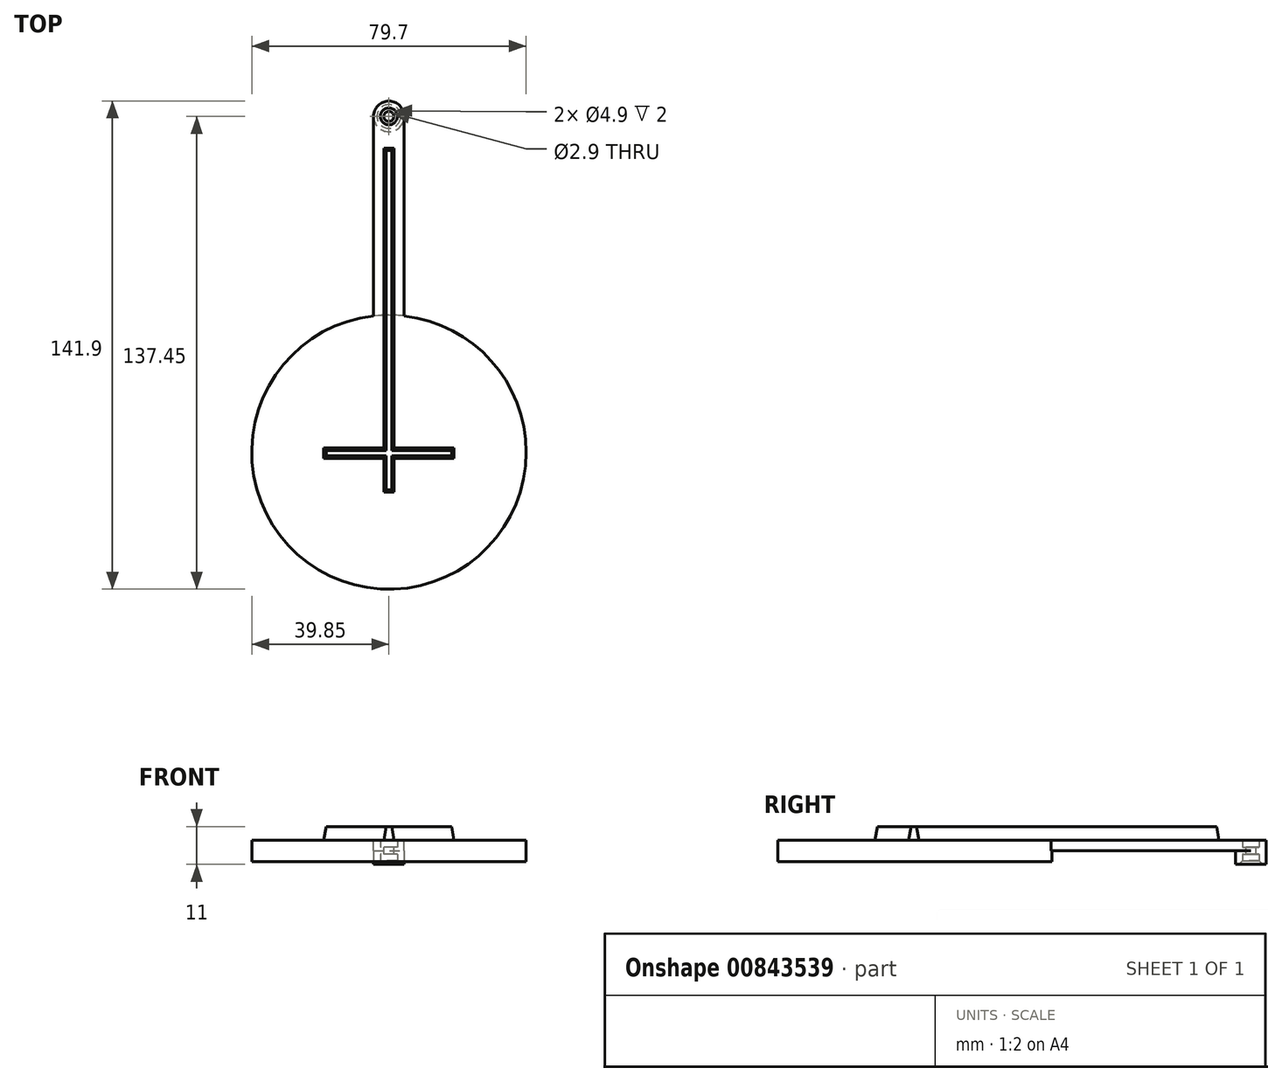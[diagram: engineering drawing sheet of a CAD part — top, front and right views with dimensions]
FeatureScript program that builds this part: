
annotation { "Feature Type Name" : "Feature", "Feature Type Description" : "" }
export const myFeature = defineFeature(function(context is Context, id is Id, definition is map)
    precondition{}
    {
        {
            var Q0;
            Q0=qCreatedBy(makeId("Top.planeOp"),FACE);
            var sketch = newSketch(context, id + "F0", { "sketchPlane" : qUnion([Q0])});
            skCircle(sketch, "E0", {"center": v(0, 0) * mm, "radius": 2.45 * mm});
            skCircle(sketch, "E1", {"center": v(0, 0) * mm, "radius": 4.45 * mm});
            skSolve(sketch);
        }
        {
            var Q0;
            Q0=makeQuery(id+"F0.imprint","IMPRINT",FACE,{"disambiguationData":[TD([[makeQuery(id+"F0.imprint","IMPRINT",EDGE,{"derivedFrom":sQuery(id+"F0.wireOp",EDGE,"E0")}),-1.0]])]});
            extrude(context, id + "F1", {"entities" : qUnion([Q0]), "depth" : 7 * mm, "offsetDistance" : 25 * mm});
        }
        {
            var Q0;
            Q0=makeQuery(id+"F1.opExtrude","CAP_FACE",FACE,{"disambiguationData":[OSD([sQuery(id+"F0.wireOp",EDGE,"E0"),sQuery(id+"F0.wireOp",EDGE,"E1")])],"isStart":false});
            var sketch = newSketch(context, id + "F2", { "sketchPlane" : qUnion([Q0])});
            skLineSegment(sketch, "E2", {"start": v(-4.45, 0) * mm, "end": v(-4.45, -58) * mm});
            skLineSegment(sketch, "E3.MirrorCS", {"start": v(4.45, 0) * mm, "end": v(4.45, -58) * mm});
            skCircle(sketch, "E4", {"center": v(0, -97.6) * mm, "radius": 39.85 * mm});
            skSolve(sketch);
        }
        {
            var Q0;
            {var subQ0=sQuery(id+"F2.wireOp",EDGE,"E2");Q0=makeQuery(id+"F2.imprint","IMPRINT",FACE,{"disambiguationData":[TD([[makeQuery(id+"F2.imprint","IMPRINT",EDGE,{"derivedFrom":subQ0}),1.0]])]});}
            var Q1;
            {var subQ0=sQuery(id+"F2.wireOp",EDGE,"E4");var subQ1=makeQuery(id+"F2.imprint","INTERSECT",VERTEX,{"derivedFrom":[sQuery(id+"F2.wireOp",EDGE,"E2"),subQ0]});Q1=makeQuery(id+"F2.imprint","IMPRINT",FACE,{"disambiguationData":[TD([[makeQuery(id+"F2.imprint","IMPRINT",EDGE,{"disambiguationData":[TD([[subQ1,1.0]])],"derivedFrom":subQ0}),1.0]])]});}
            extrude(context, id + "F3", {"entities" : qUnion([Q0, Q1]), "operationType" : NewBodyOperationType.ADD, "oppositeDirection" : true, "depth" : 3 * mm, "offsetDistance" : 25 * mm});
        }
        {
            var Q0;
            {var subQ0=sQuery(id+"F0.wireOp",EDGE,"E1");Q0=makeQuery(id+"F3.boolean.opBoolean","MERGE",FACE,{"derivedFrom":[makeQuery(id+"F1.opExtrude","CAP_FACE",FACE,{"disambiguationData":[OSD([sQuery(id+"F0.wireOp",EDGE,"E0"),subQ0])],"isStart":false}),makeQuery(id+"F3.opExtrude","CAP_FACE",FACE,{"disambiguationData":[OSD([subQ0,sQuery(id+"F2.wireOp",EDGE,"E2"),sQuery(id+"F2.wireOp",EDGE,"E3.MirrorCS"),sQuery(id+"F2.wireOp",EDGE,"E4")])],"isStart":true})]});}
            var sketch = newSketch(context, id + "F4", { "sketchPlane" : qUnion([Q0])});
            skCircle(sketch, "E5", {"center": v(0, 0) * mm, "radius": 1.45 * mm});
            skSolve(sketch);
        }
        {
            var Q0;
            Q0=makeQuery(id+"F4.imprint","IMPRINT",FACE,{"disambiguationData":[TD([[makeQuery(id+"F4.imprint","IMPRINT",EDGE,{"derivedFrom":sQuery(id+"F4.wireOp",EDGE,"E5")}),-1.0]])]});
            extrude(context, id + "F5", {"entities" : qUnion([Q0]), "operationType" : NewBodyOperationType.ADD, "oppositeDirection" : true, "depth" : 4 * mm, "offsetDistance" : 25 * mm, "hasSecondDirection" : true, "secondDirectionOppositeDirection" : true, "secondDirectionDepth" : 2 * mm});
        }
        {
            var Q0;
            {var subQ0=sQuery(id+"F0.wireOp",EDGE,"E1");Q0=makeQuery(id+"F3.boolean.opBoolean","MERGE",FACE,{"derivedFrom":[makeQuery(id+"F1.opExtrude","CAP_FACE",FACE,{"disambiguationData":[OSD([sQuery(id+"F0.wireOp",EDGE,"E0"),subQ0])],"isStart":false}),makeQuery(id+"F3.opExtrude","CAP_FACE",FACE,{"disambiguationData":[OSD([subQ0,sQuery(id+"F2.wireOp",EDGE,"E2"),sQuery(id+"F2.wireOp",EDGE,"E3.MirrorCS"),sQuery(id+"F2.wireOp",EDGE,"E4")])],"isStart":true})]});}
            var sketch = newSketch(context, id + "F6", { "sketchPlane" : qUnion([Q0])});
            skLineSegment(sketch, "E6", {"start": v(0, -137.45) * mm, "end": v(0, 4.45) * mm, "construction": true});
            skLineSegment(sketch, "E7.bottom", {"start": v(1.5, -9.24) * mm, "end": v(-1.5, -9.24) * mm});
            skLineSegment(sketch, "E7.top", {"start": v(1.5, -109.24) * mm, "end": v(-1.5, -109.24) * mm});
            skLineSegment(sketch, "E7.left", {"start": v(1.5, -9.24) * mm, "end": v(1.5, -109.24) * mm});
            skLineSegment(sketch, "E7.right", {"start": v(-1.5, -9.24) * mm, "end": v(-1.5, -109.24) * mm});
            skPoint(sketch, "E8", {"position": v(0, -9.24) * mm});
            skLineSegment(sketch, "E9.bottom", {"start": v(18.95, -96.41) * mm, "end": v(-18.95, -96.41) * mm});
            skLineSegment(sketch, "E9.top", {"start": v(18.95, -99.41) * mm, "end": v(-18.95, -99.41) * mm});
            skLineSegment(sketch, "E9.left", {"start": v(18.95, -96.41) * mm, "end": v(18.95, -99.41) * mm});
            skLineSegment(sketch, "E9.right", {"start": v(-18.95, -96.41) * mm, "end": v(-18.95, -99.41) * mm});
            skPoint(sketch, "E10", {"position": v(0, -99.41) * mm});
            skSolve(sketch);
        }
        {
            var Q0;
            Q0 = qSketchRegion(id + "F6", true);
            extrude(context, id + "F7", {"entities" : qUnion([Q0]), "depth" : 4 * mm, "offsetDistance" : 25 * mm, "hasDraft" : true, "draftAngle" : 10 * degree, "draftPullDirection" : true});
        }
        {
            var Q0;
            Q0=makeQuery(id+"F3.opExtrude","CAP_FACE",FACE,{"disambiguationData":[OSD([sQuery(id+"F0.wireOp",EDGE,"E1"),sQuery(id+"F2.wireOp",EDGE,"E2"),sQuery(id+"F2.wireOp",EDGE,"E3.MirrorCS"),sQuery(id+"F2.wireOp",EDGE,"E4")])],"isStart":false});
            var sketch = newSketch(context, id + "F8", { "sketchPlane" : qUnion([Q0])});
            skCircle(sketch, "E11", {"center": v(0, 97.6) * mm, "radius": 39.85 * mm});
            skSolve(sketch);
        }
        {
            var Q0;
            Q0 = qSketchRegion(id + "F8", true);
            extrude(context, id + "F9", {"entities" : qUnion([Q0]), "operationType" : NewBodyOperationType.ADD, "depth" : 3.17 * mm, "offsetDistance" : 25 * mm});
        }
        {
            var Q0;
            Q0=makeQuery(id+"F1.opExtrude","CAP_EDGE",EDGE,{"disambiguationData":[OSD([sQuery(id+"F0.wireOp",EDGE,"E0")])],"isStart":true});
            chamfer(context, id + "F10", {"entities" : qUnion([Q0]), "width" : 1 * mm, "tangentPropagation" : true});
        }
    });
